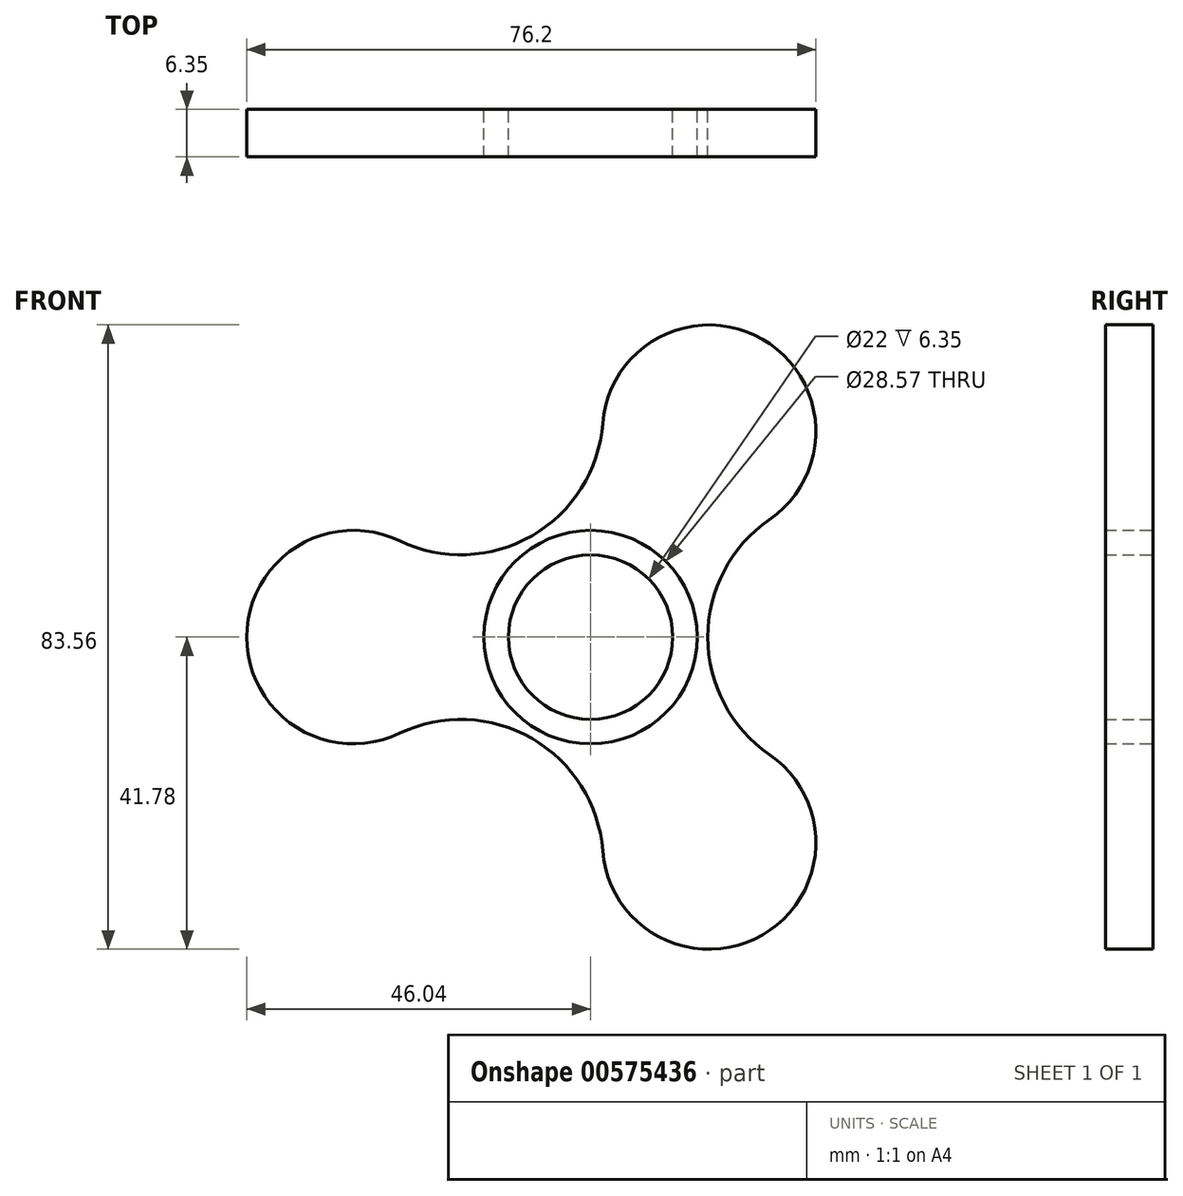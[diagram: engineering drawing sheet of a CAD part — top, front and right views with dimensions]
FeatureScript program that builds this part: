
annotation { "Feature Type Name" : "Feature", "Feature Type Description" : "" }
export const myFeature = defineFeature(function(context is Context, id is Id, definition is map)
    precondition{}
    {
        {
            var Q0;
            Q0=qCreatedBy(makeId("Front.planeOp"),FACE);
            var sketch = newSketch(context, id + "F0", { "sketchPlane" : qUnion([Q0])});
            skCircle(sketch, "E0", {"center": v(0, 0) * mm, "radius": 14.29 * mm});
            skCircle(sketch, "E1", {"center": v(0, 0) * mm, "radius": 11 * mm});
            skCircle(sketch, "E2", {"center": v(-31.75, 0) * mm, "radius": 14.29 * mm});
            skCircle(sketch, "E3", {"center": v(-31.75, 0) * mm, "radius": 11 * mm});
            skCircle(sketch, "E4.1.0", {"center": v(15.87, -27.5) * mm, "radius": 11 * mm});
            skCircle(sketch, "E4.1.1", {"center": v(15.87, -27.5) * mm, "radius": 14.29 * mm});
            skCircle(sketch, "E4.2.0", {"center": v(15.88, 27.5) * mm, "radius": 11 * mm});
            skCircle(sketch, "E4.2.1", {"center": v(15.88, 27.5) * mm, "radius": 14.29 * mm});
            skSolve(sketch);
        }
        {
            var Q0;
            Q0=qCreatedBy(makeId("Front.planeOp"),FACE);
            var sketch = newSketch(context, id + "F1", { "sketchPlane" : qUnion([Q0])});
            skArc(sketch, "E5", {"start": v(23.95, 15.71) * mm, "mid": v(15.68, 0) * mm, "end": v(23.95, -15.71) * mm});
            skArc(sketch, "E6", {"start": v(-25.58, 12.89) * mm, "mid": v(-7.84, 13.58) * mm, "end": v(1.63, 28.6) * mm});
            skArc(sketch, "E7", {"start": v(1.63, -28.6) * mm, "mid": v(-7.84, -13.58) * mm, "end": v(-25.58, -12.89) * mm});
            skCircle(sketch, "E8.0", {"center": v(15.88, 27.5) * mm, "radius": 14.29 * mm});
            skCircle(sketch, "E9.0", {"center": v(-31.75, 0) * mm, "radius": 14.29 * mm});
            skCircle(sketch, "E10.0", {"center": v(15.87, -27.5) * mm, "radius": 14.29 * mm});
            skCircle(sketch, "E11.0", {"center": v(0, 0) * mm, "radius": 14.29 * mm});
            skSolve(sketch);
        }
        {
            var Q0;
            Q0 = qSketchRegion(id + "F1", true);
            var Q1;
            Q1=makeQuery(id+"F0.imprint","IMPRINT",FACE,{"disambiguationData":[TD([[makeQuery(id+"F0.imprint","IMPRINT",EDGE,{"derivedFrom":sQuery(id+"F0.wireOp",EDGE,"E0")}),1.0]])]});
            extrude(context, id + "F2", {"entities" : qUnion([Q0, Q1]), "depth" : 6.35 * mm, "offsetDistance" : 25.4 * mm});
        }
    });
